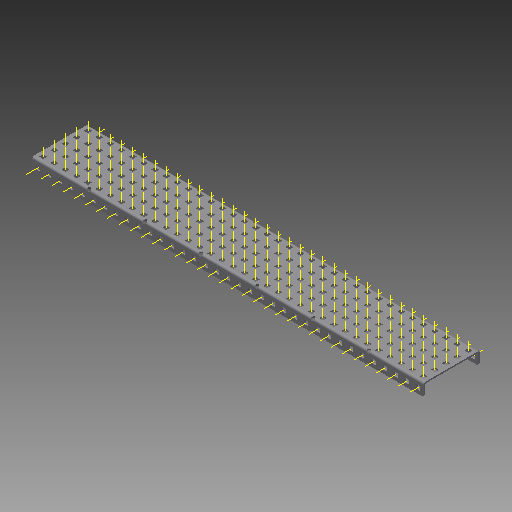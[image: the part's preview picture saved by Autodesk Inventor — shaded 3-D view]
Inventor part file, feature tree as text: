
AUTODESK INVENTOR PART (.ipt)
format: ipt  version: 2017 (Build 210142000, 142)  size: 2,832,896 bytes
history: native  units: in
note: dims shown in document units (in); Inventor stores cm internally (conversion verified against a paired STEP export)
features: other x251, pattern_linear x2, sheet_metal_op x1, extrude x1, imported_body x1, sketch x1
ambient origin geometry x8: Origin, YZ Plane, XZ Plane, XY Plane, X Axis, Y Axis, Z Axis, Center Point
bodies: Body1 (feature_tree)
feature tree (257):
  sheet_metal_op  "Fold1"
  other  "C-Channel"
  extrude  "length cut"  Depth=0.5in
  other  "top axis"
  other  "front axis"
  other  "back axis"
  pattern_linear  "top axes"  Spacing1=0.5in  [1 undecoded]
  pattern_linear  "horiz axes"  Spacing1=0.0in  [1 undecoded]
  other  "right plane"
  imported_body  "Base1"
  sketch  "Sketch1"  dims[d1=0.0in d4=0.5in d5=1.9685in d7=0.5in d10=0.5in d11=0.0in d12=0.0in d13=0.0in d14=-17.5in d15=0.0in d16=0.0in]
  other  "Work Point1"
  other  "Work Axis6"
  other  "Work Axis11"
  other  "Work Axis16"
  other  "Work Axis21"
  other  "Work Point2"
  other  "Work Point3"
  other  "Work Axis36"
  other  "Work Axis37"
  other  "Work Axis38"
  other  "Work Axis39"
  other  "Work Axis40"
  other  "Work Axis41"
  other  "Work Axis60"
  other  "Work Axis61"
  other  "Work Axis62"
  other  "Work Axis63"
  other  "Work Axis64"
  other  "Work Axis65"
  other  "Work Axis84"
  other  "Work Axis85"
  other  "Work Axis86"
  other  "Work Axis87"
  other  "Work Axis88"
  other  "Work Axis89"
  other  "Work Axis108"
  other  "Work Axis109"
  other  "Work Axis110"
  other  "Work Axis111"
  other  "Work Axis112"
  other  "Work Axis113"
  other  "Work Axis132"
  other  "Work Axis133"
  other  "Work Axis134"
  other  "Work Axis135"
  other  "Work Axis136"
  other  "Work Axis137"
  other  "Work Axis156"
  other  "Work Axis157"
  other  "Work Axis158"
  other  "Work Axis159"
  other  "Work Axis160"
  other  "Work Axis161"
  other  "Work Axis180"
  other  "Work Axis181"
  other  "Work Axis182"
  other  "Work Axis183"
  other  "Work Axis184"
  other  "Work Axis185"
  other  "Work Axis204"
  other  "Work Axis205"
  other  "Work Axis206"
  other  "Work Axis207"
  other  "Work Axis208"
  other  "Work Axis209"
  other  "Work Axis210"
  other  "Work Axis211"
  other  "Work Axis212"
  other  "Work Axis213"
  other  "Work Axis214"
  other  "Work Axis215"
  other  "Work Axis216"
  other  "Work Axis232"
  other  "Work Axis233"
  other  "Work Axis234"
  other  "Work Axis235"
  other  "Work Axis236"
  other  "Work Axis237"
  other  "Work Axis238"
  other  "Work Axis239"
  other  "Work Axis240"
  other  "Work Axis241"
  other  "Work Axis242"
  other  "Work Axis243"
  other  "Work Axis244"
  other  "Work Axis260"
  other  "Work Axis261"
  other  "Work Axis262"
  other  "Work Axis263"
  other  "Work Axis264"
  other  "Work Axis265"
  other  "Work Axis266"
  other  "Work Axis267"
  other  "Work Axis268"
  other  "Work Axis269"
  other  "Work Axis270"
  other  "Work Axis271"
  other  "Work Axis272"
  other  "Work Axis288"
  other  "Work Axis289"
  other  "Work Axis290"
  other  "Work Axis291"
  other  "Work Axis292"
  other  "Work Axis293"
  other  "Work Axis294"
  other  "Work Axis295"
  other  "Work Axis296"
  other  "Work Axis297"
  other  "Work Axis298"
  other  "Work Axis299"
  other  "Work Axis300"
  other  "Work Axis316"
  other  "Work Axis317"
  other  "Work Axis318"
  other  "Work Axis319"
  other  "Work Axis320"
  other  "Work Axis321"
  other  "Work Axis322"
  other  "Work Axis323"
  other  "Work Axis324"
  other  "Work Axis325"
  other  "Work Axis326"
  other  "Work Axis327"
  other  "Work Axis328"
  other  "Work Axis344"
  other  "Work Axis345"
  other  "Work Axis346"
  other  "Work Axis347"
  other  "Work Axis348"
  other  "Work Axis349"
  other  "Work Axis350"
  other  "Work Axis351"
  other  "Work Axis352"
  other  "Work Axis353"
  other  "Work Axis354"
  other  "Work Axis355"
  other  "Work Axis356"
  other  "Work Axis372"
  other  "Work Axis373"
  other  "Work Axis374"
  other  "Work Axis375"
  other  "Work Axis376"
  other  "Work Axis377"
  other  "Work Axis378"
  other  "Work Axis379"
  other  "Work Axis380"
  other  "Work Axis381"
  other  "Work Axis382"
  other  "Work Axis383"
  other  "Work Axis384"
  other  "left plane"
  other  "Work Axis400"
  other  "Work Axis401"
  other  "Work Axis402"
  other  "Work Axis403"
  other  "Work Axis404"
  other  "Work Axis405"
  other  "Work Axis406"
  other  "Work Axis407"
  other  "Work Axis408"
  other  "Work Axis409"
  other  "Work Axis410"
  other  "Work Axis411"
  other  "Work Axis412"
  other  "Work Axis413"
  other  "Work Axis414"
  other  "Work Axis415"
  other  "Work Axis416"
  other  "Work Axis417"
  other  "Work Axis418"
  other  "Work Axis419"
  other  "Work Axis420"
  other  "Work Axis421"
  other  "Work Axis422"
  other  "Work Axis423"
  other  "Work Axis424"
  other  "Work Axis425"
  other  "Work Axis426"
  other  "Work Axis427"
  other  "Work Axis428"
  other  "Work Axis429"
  other  "Work Axis430"
  other  "Work Axis431"
  other  "Work Axis432"
  other  "Work Axis433"
  other  "Work Axis434"
  other  "Work Axis435"
  other  "Work Axis436"
  other  "Work Axis437"
  other  "Work Axis438"
  other  "Work Axis439"
  other  "Work Axis440"
  other  "Work Axis441"
  other  "Work Axis442"
  other  "Work Axis443"
  other  "Work Axis444"
  other  "Work Axis445"
  other  "Work Axis446"
  other  "Work Axis447"
  other  "Work Axis448"
  other  "Work Axis449"
  other  "Work Axis450"
  other  "Work Axis451"
  other  "Work Axis452"
  other  "Work Axis453"
  other  "Work Axis454"
  other  "Work Axis455"
  other  "Work Axis456"
  other  "Work Axis457"
  other  "Work Axis458"
  other  "Work Axis459"
  other  "Work Axis460"
  other  "Work Axis461"
  other  "Work Axis462"
  other  "Work Axis463"
  other  "Work Axis464"
  other  "Work Axis465"
  other  "Work Axis466"
  other  "Work Axis467"
  other  "Work Axis468"
  other  "Work Axis469"
  other  "Work Axis470"
  other  "Work Axis471"
  other  "Work Axis472"
  other  "Work Axis473"
  other  "Work Axis474"
  other  "Work Axis475"
  other  "Work Axis476"
  other  "Work Axis477"
  other  "Work Axis478"
  other  "Work Axis479"
  other  "Work Axis480"
  other  "Work Axis481"
  other  "Work Axis482"
  other  "Work Axis483"
  other  "Work Axis484"
  other  "Work Axis485"
  other  "Work Axis486"
  other  "Work Axis487"
  other  "Work Axis488"
  other  "Work Axis489"
  other  "Work Axis490"
  other  "Work Axis491"
  other  "Work Axis492"
  other  "Work Axis493"
  other  "Work Axis494"
  other  "Work Axis495"
  other  "Work Axis496"
  other  "Work Axis497"
  other  "Work Axis498"
  other  "Work Axis499"
  other  "Work Axis500"
  other  "Work Axis501"
  other  "Work Axis502"
  other  "Work Axis503"
  other  "Work Axis504"
note: 2 required parameter values undecoded (feature->parameter linkage not recoverable at this tier; creation-order binding heuristic only, values carry confidence <= 0.55)
